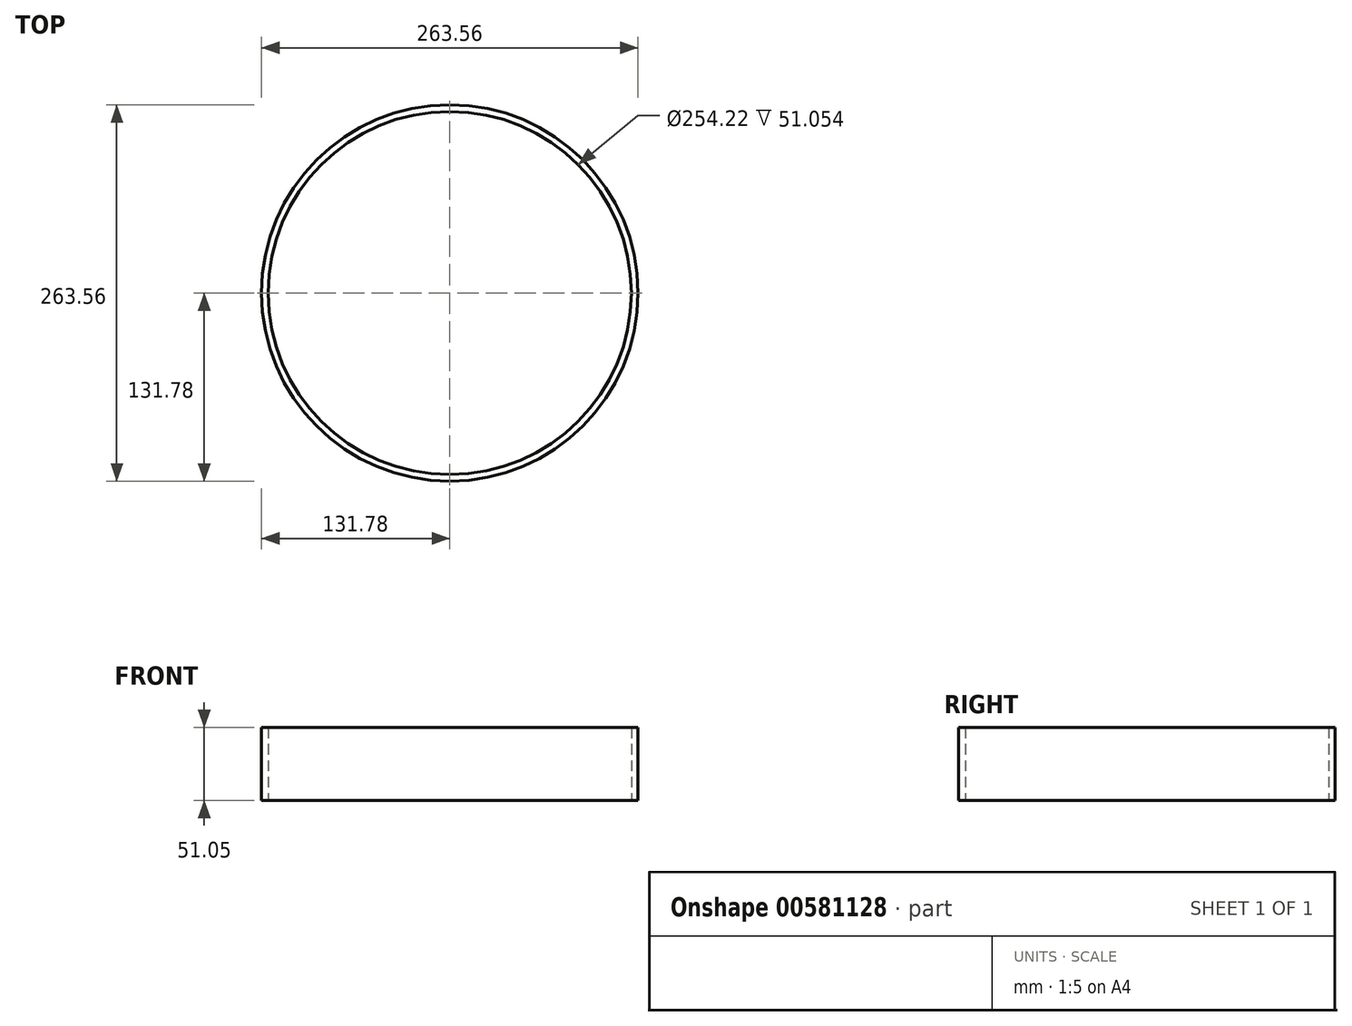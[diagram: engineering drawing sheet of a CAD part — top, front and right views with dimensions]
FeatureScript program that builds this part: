
annotation { "Feature Type Name" : "Feature", "Feature Type Description" : "" }
export const myFeature = defineFeature(function(context is Context, id is Id, definition is map)
    precondition{}
    {
        {
            var Q0;
            Q0=qCreatedBy(makeId("Top.planeOp"),FACE);
            var sketch = newSketch(context, id + "F0", { "sketchPlane" : qUnion([Q0])});
            skCircle(sketch, "E0", {"center": v(0, 0) * mm, "radius": 131.78 * mm});
            skCircle(sketch, "E1", {"center": v(0, 0) * mm, "radius": 127.11 * mm});
            skSolve(sketch);
        }
        {
            var Q0;
            Q0 = qSketchRegion(id + "F0", true);
            extrude(context, id + "F1", {"entities" : qUnion([Q0]), "depth" : 51.05 * mm, "offsetDistance" : 25.4 * mm});
        }
    });
